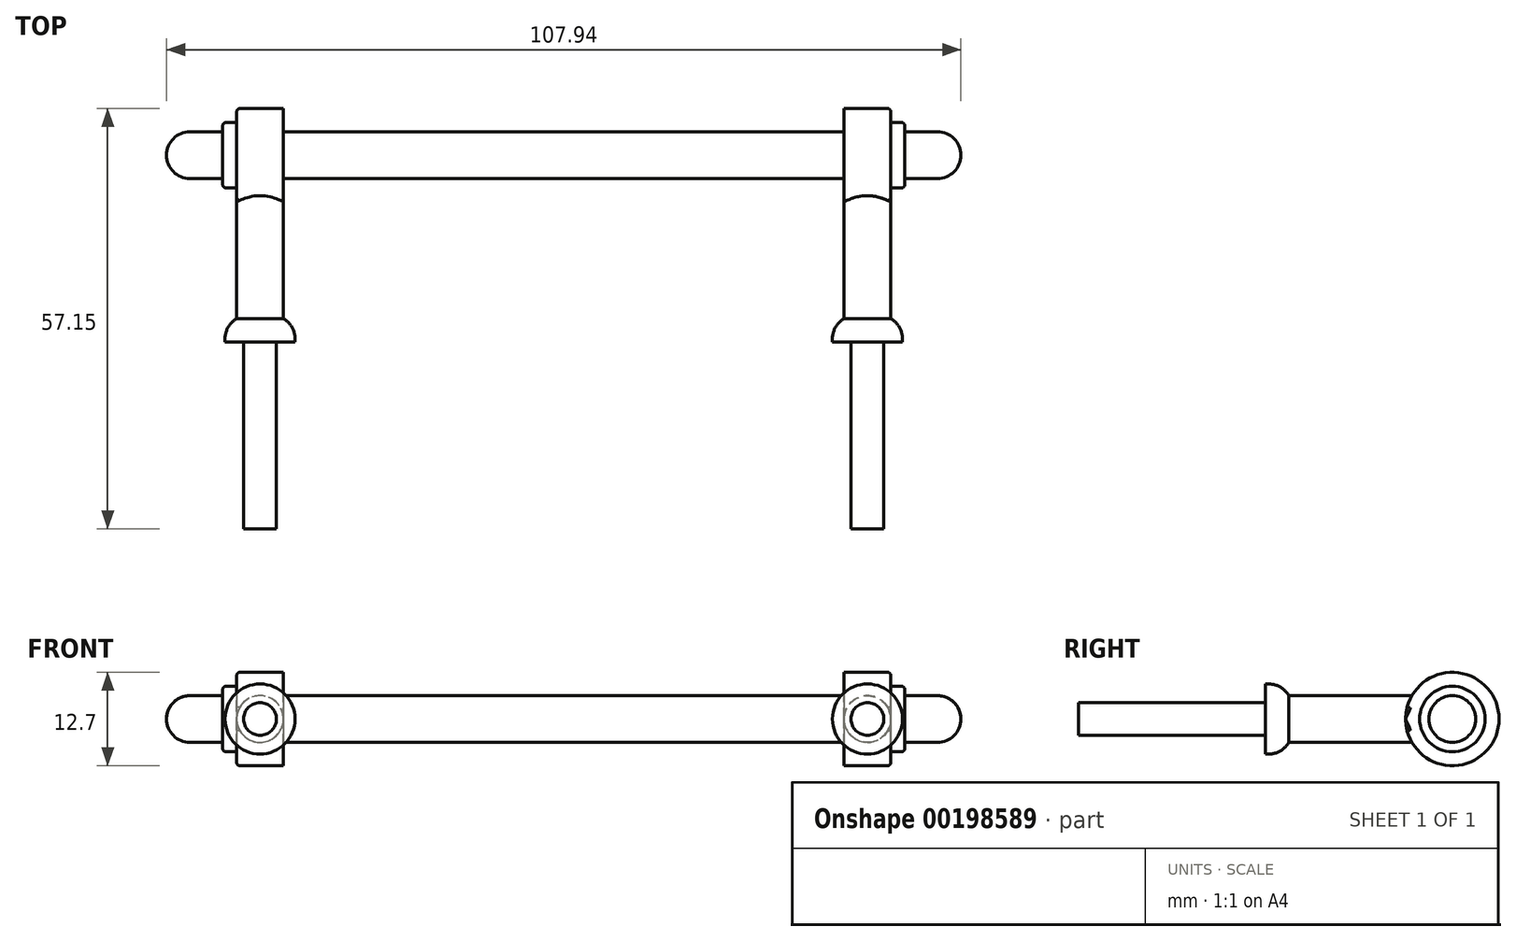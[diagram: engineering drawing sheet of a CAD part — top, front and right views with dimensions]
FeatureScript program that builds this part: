
annotation { "Feature Type Name" : "Feature", "Feature Type Description" : "" }
export const myFeature = defineFeature(function(context is Context, id is Id, definition is map)
    precondition{}
    {
        {
            var Q0;
            Q0=qCreatedBy(makeId("Front.planeOp"),FACE);
            var sketch = newSketch(context, id + "F0", { "sketchPlane" : qUnion([Q0])});
            skLineSegment(sketch, "E0", {"start": v(0, 3.18) * mm, "end": v(-38.1, 3.18) * mm});
            skLineSegment(sketch, "E1", {"start": v(-38.1, 3.18) * mm, "end": v(-38.1, 6.35) * mm});
            skLineSegment(sketch, "E2", {"start": v(-38.1, 6.35) * mm, "end": v(-44.45, 6.35) * mm});
            skLineSegment(sketch, "E3", {"start": v(-44.45, 6.35) * mm, "end": v(-44.45, 4.44) * mm});
            skLineSegment(sketch, "E4", {"start": v(-44.45, 4.44) * mm, "end": v(-46.35, 4.44) * mm});
            skLineSegment(sketch, "E5", {"start": v(-46.35, 4.44) * mm, "end": v(-46.35, 3.18) * mm});
            skLineSegment(sketch, "E6", {"start": v(-46.35, 3.18) * mm, "end": v(-50.8, 3.18) * mm});
            skLineSegment(sketch, "E7", {"start": v(-50.8, 0) * mm, "end": v(0, 0) * mm});
            skArc(sketch, "E8", {"start": v(-50.8, 3.18) * mm, "mid": v(-53.05, 2.25) * mm, "end": v(-53.97, 0) * mm});
            skLineSegment(sketch, "E9", {"start": v(-53.97, 0) * mm, "end": v(-50.8, 0) * mm});
            skLineSegment(sketch, "E10.MirrorCS", {"start": v(46.35, 4.44) * mm, "end": v(46.35, 3.18) * mm});
            skLineSegment(sketch, "E11.MirrorCS", {"start": v(44.45, 6.35) * mm, "end": v(44.45, 4.44) * mm});
            skLineSegment(sketch, "E12.MirrorCS", {"start": v(44.45, 4.44) * mm, "end": v(46.35, 4.44) * mm});
            skLineSegment(sketch, "E13.MirrorCS", {"start": v(53.97, 0) * mm, "end": v(50.8, 0) * mm});
            skArc(sketch, "E14.MirrorCS", {"start": v(50.8, 3.18) * mm, "mid": v(53.05, 2.25) * mm, "end": v(53.97, 0) * mm});
            skLineSegment(sketch, "E15.MirrorCS", {"start": v(0, 3.18) * mm, "end": v(38.1, 3.18) * mm});
            skLineSegment(sketch, "E16.MirrorCS", {"start": v(50.8, 0) * mm, "end": v(0, 0) * mm});
            skLineSegment(sketch, "E17.MirrorCS", {"start": v(46.35, 3.18) * mm, "end": v(50.8, 3.18) * mm});
            skLineSegment(sketch, "E18.MirrorCS", {"start": v(38.1, 6.35) * mm, "end": v(44.45, 6.35) * mm});
            skLineSegment(sketch, "E19.MirrorCS", {"start": v(38.1, 3.18) * mm, "end": v(38.1, 6.35) * mm});
            skSolve(sketch);
        }
        {
            var Q0;
            Q0 = qSketchRegion(id + "F0", true);
            var Q1;
            Q1=sQuery(id+"F0.wireOp",EDGE,"E7");
            revolve(context, id + "F1", {"entities" : qUnion([Q0]), "axis" : qUnion([Q1]), "revolveType" : RevolveType.FULL});
        }
        {
            var Q0;
            Q0=qCreatedBy(makeId("Front.planeOp"),FACE);
            cPlane(context, id + "F2", {"entities" : qUnion([Q0]), "cplaneType" : CPlaneType.OFFSET, "offset" : 6.35 * mm, "width" : 152.4 * mm, "height" : 152.4 * mm});
        }
        {
            var Q0;
            Q0=qCreatedBy(id+"F2.planeOp",FACE);
            var sketch = newSketch(context, id + "F3", { "sketchPlane" : qUnion([Q0])});
            skCircle(sketch, "E20", {"center": v(-41.27, 0) * mm, "radius": 3.18 * mm});
            skCircle(sketch, "E21", {"center": v(41.27, 0) * mm, "radius": 3.18 * mm});
            skSolve(sketch);
        }
        {
            var Q0;
            Q0 = qSketchRegion(id + "F3", true);
            extrude(context, id + "F4", {"entities" : qUnion([Q0]), "operationType" : NewBodyOperationType.ADD, "depth" : 19.05 * mm, "hasSecondDirection" : true, "secondDirectionOppositeDirection" : true, "secondDirectionDepth" : 6.35 * mm});
        }
        {
            var Q0;
            Q0=makeQuery(id+"F4.opExtrude","CAP_FACE",FACE,{"disambiguationData":[OSD([sQuery(id+"F3.wireOp",EDGE,"E20")])],"isStart":false});
            var sketch = newSketch(context, id + "F5", { "sketchPlane" : qUnion([Q0])});
            skCircle(sketch, "E22", {"center": v(-41.27, 0) * mm, "radius": 2.22 * mm});
            skCircle(sketch, "E23", {"center": v(41.27, 0) * mm, "radius": 2.22 * mm});
            skSolve(sketch);
        }
        {
            var Q0;
            Q0 = qSketchRegion(id + "F5", true);
            extrude(context, id + "F6", {"entities" : qUnion([Q0]), "operationType" : NewBodyOperationType.ADD, "depth" : 25.4 * mm});
        }
        {
            var Q0;
            Q0=makeQuery(id+"F4.opExtrude","CAP_FACE",FACE,{"disambiguationData":[OSD([sQuery(id+"F3.wireOp",EDGE,"E20")])],"isStart":false});
            var sketch = newSketch(context, id + "F7", { "sketchPlane" : qUnion([Q0])});
            skCircle(sketch, "E24", {"center": v(-41.27, 0) * mm, "radius": 4.76 * mm});
            skCircle(sketch, "E25", {"center": v(41.27, 0) * mm, "radius": 4.76 * mm});
            skSolve(sketch);
        }
        {
            var Q0;
            Q0 = qSketchRegion(id + "F7", true);
            extrude(context, id + "F8", {"entities" : qUnion([Q0]), "operationType" : NewBodyOperationType.ADD, "oppositeDirection" : true, "depth" : 3.17 * mm});
        }
        {
            var Q0;
            Q0=makeQuery(id+"F1.opRevolve","SWEPT_EDGE",EDGE,{"disambiguationData":[OSD([sQuery(id+"F0.wireOp",EDGE,"E4"),sQuery(id+"F0.wireOp",EDGE,"E5")])]});
            var Q1;
            Q1=makeQuery(id+"F1.opRevolve","SWEPT_EDGE",EDGE,{"disambiguationData":[OSD([sQuery(id+"F0.wireOp",EDGE,"E2"),sQuery(id+"F0.wireOp",EDGE,"E3")])]});
            var Q2;
            Q2=makeQuery(id+"F1.opRevolve","SWEPT_EDGE",EDGE,{"disambiguationData":[OSD([sQuery(id+"F0.wireOp",EDGE,"E11.MirrorCS"),sQuery(id+"F0.wireOp",EDGE,"E18.MirrorCS")])]});
            var Q3;
            Q3=makeQuery(id+"F1.opRevolve","SWEPT_EDGE",EDGE,{"disambiguationData":[OSD([sQuery(id+"F0.wireOp",EDGE,"E10.MirrorCS"),sQuery(id+"F0.wireOp",EDGE,"E12.MirrorCS")])]});
            fillet(context, id + "F9", {"entities" : qUnion([Q0, Q1, Q2, Q3]), "radius" : 0.44 * mm, "tangentPropagation" : true, "allowEdgeOverflow" : false});
        }
        {
            var Q0;
            Q0=makeQuery(id+"F8.opExtrude","CAP_EDGE",EDGE,{"disambiguationData":[OSD([sQuery(id+"F7.wireOp",EDGE,"E25")])],"isStart":false});
            var Q1;
            Q1=makeQuery(id+"F8.opExtrude","CAP_EDGE",EDGE,{"disambiguationData":[OSD([sQuery(id+"F7.wireOp",EDGE,"E24")])],"isStart":false});
            fillet(context, id + "F10", {"entities" : qUnion([Q0, Q1]), "radius" : 3.17 * mm, "tangentPropagation" : true, "allowEdgeOverflow" : false});
        }
    });
